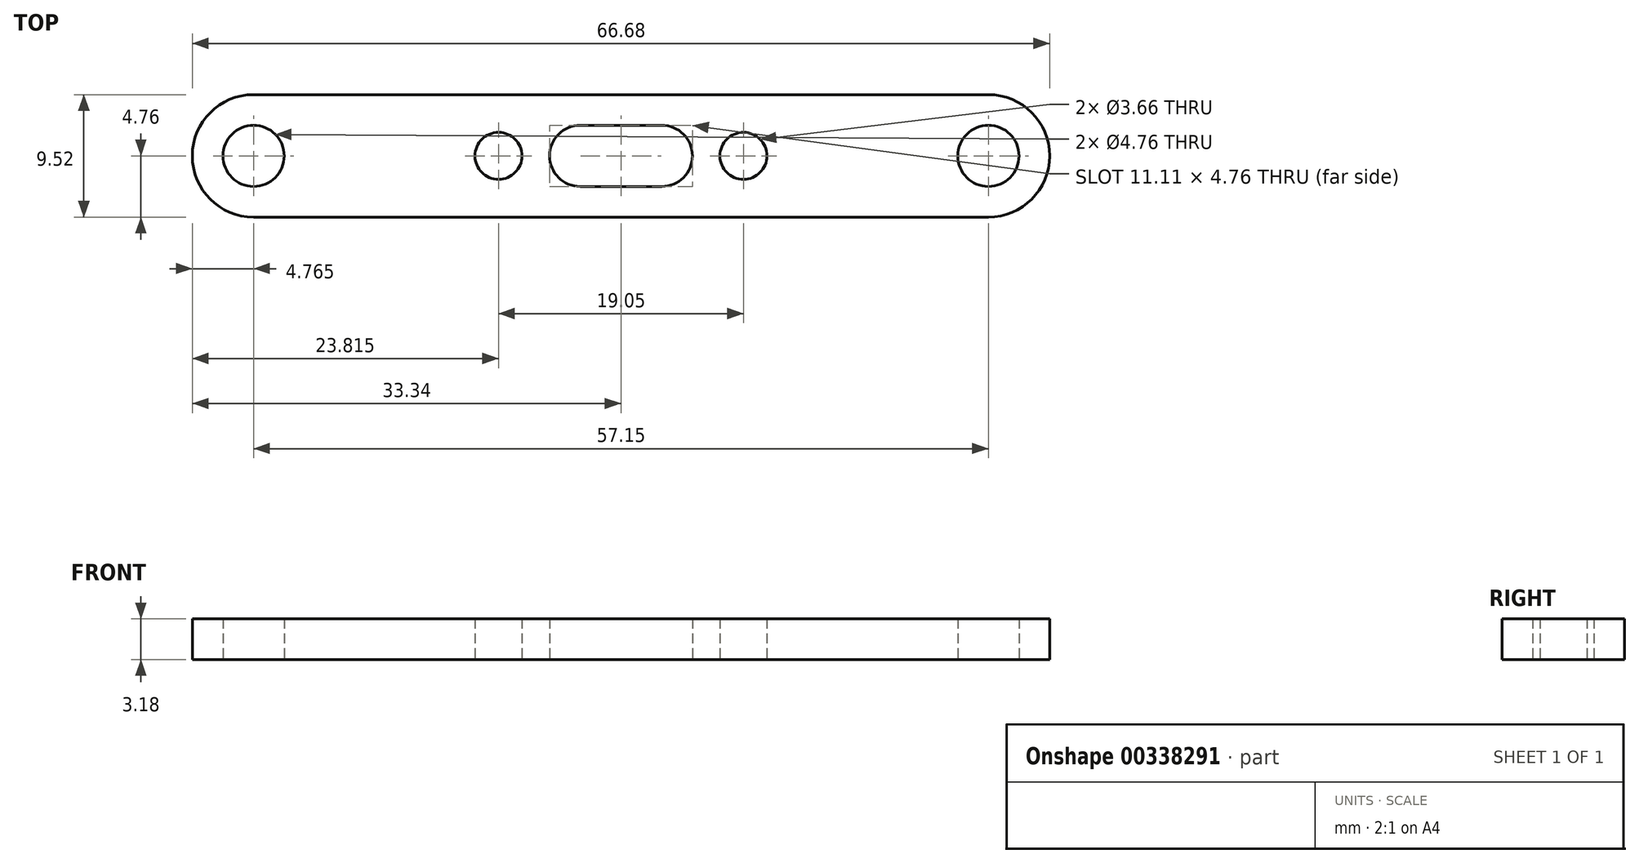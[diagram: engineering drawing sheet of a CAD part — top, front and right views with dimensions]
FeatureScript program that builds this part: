
annotation { "Feature Type Name" : "Feature", "Feature Type Description" : "" }
export const myFeature = defineFeature(function(context is Context, id is Id, definition is map)
    precondition{}
    {
        {
            var Q0;
            Q0=qCreatedBy(makeId("Top.planeOp"),FACE);
            var sketch = newSketch(context, id + "F0", { "sketchPlane" : qUnion([Q0])});
            skLineSegment(sketch, "E0.bottom", {"start": v(3.18, -2.38) * mm, "end": v(-3.18, -2.38) * mm});
            skLineSegment(sketch, "E0.top", {"start": v(3.17, 2.38) * mm, "end": v(-3.18, 2.38) * mm});
            skLineSegment(sketch, "E0.left", {"start": v(3.18, -2.38) * mm, "end": v(3.18, 2.38) * mm, "construction": true});
            skLineSegment(sketch, "E0.right", {"start": v(-3.18, -2.38) * mm, "end": v(-3.18, 2.38) * mm, "construction": true});
            skPoint(sketch, "E0.middle", {"position": v(0, 0) * mm});
            skArc(sketch, "E1", {"start": v(3.18, -2.38) * mm, "mid": v(5.56, 0) * mm, "end": v(3.18, 2.38) * mm});
            skArc(sketch, "E2", {"start": v(-3.18, 2.38) * mm, "mid": v(-5.56, 0) * mm, "end": v(-3.18, -2.38) * mm});
            skCircle(sketch, "E3", {"center": v(9.53, 0) * mm, "radius": 1.83 * mm});
            skLineSegment(sketch, "E4", {"start": v(-9.53, 0) * mm, "end": v(9.53, 0) * mm, "construction": true});
            skCircle(sketch, "E5", {"center": v(-9.53, 0) * mm, "radius": 1.83 * mm});
            skLineSegment(sketch, "E6", {"start": v(9.52, 0) * mm, "end": v(28.58, 0) * mm, "construction": true});
            skCircle(sketch, "E7", {"center": v(28.58, 0) * mm, "radius": 2.38 * mm});
            skLineSegment(sketch, "E8.bottom", {"start": v(28.58, 4.76) * mm, "end": v(-28.58, 4.76) * mm});
            skLineSegment(sketch, "E8.top", {"start": v(28.58, -4.76) * mm, "end": v(-28.58, -4.76) * mm});
            skLineSegment(sketch, "E8.left", {"start": v(28.58, 4.76) * mm, "end": v(28.58, -4.76) * mm, "construction": true});
            skLineSegment(sketch, "E8.right", {"start": v(-28.58, 4.76) * mm, "end": v(-28.58, -4.76) * mm, "construction": true});
            skLineSegment(sketch, "E9", {"start": v(-9.53, 0) * mm, "end": v(-28.58, 0) * mm, "construction": true});
            skArc(sketch, "E10", {"start": v(28.58, -4.76) * mm, "mid": v(33.34, 0) * mm, "end": v(28.58, 4.76) * mm});
            skArc(sketch, "E11", {"start": v(-28.58, 4.76) * mm, "mid": v(-33.34, 0) * mm, "end": v(-28.58, -4.76) * mm});
            skCircle(sketch, "E12", {"center": v(-28.58, 0) * mm, "radius": 2.38 * mm});
            skSolve(sketch);
        }
        {
            var Q0;
            Q0 = qSketchRegion(id + "F0", true);
            extrude(context, id + "F1", {"entities" : qUnion([Q0]), "depth" : 3.17 * mm});
        }
    });
